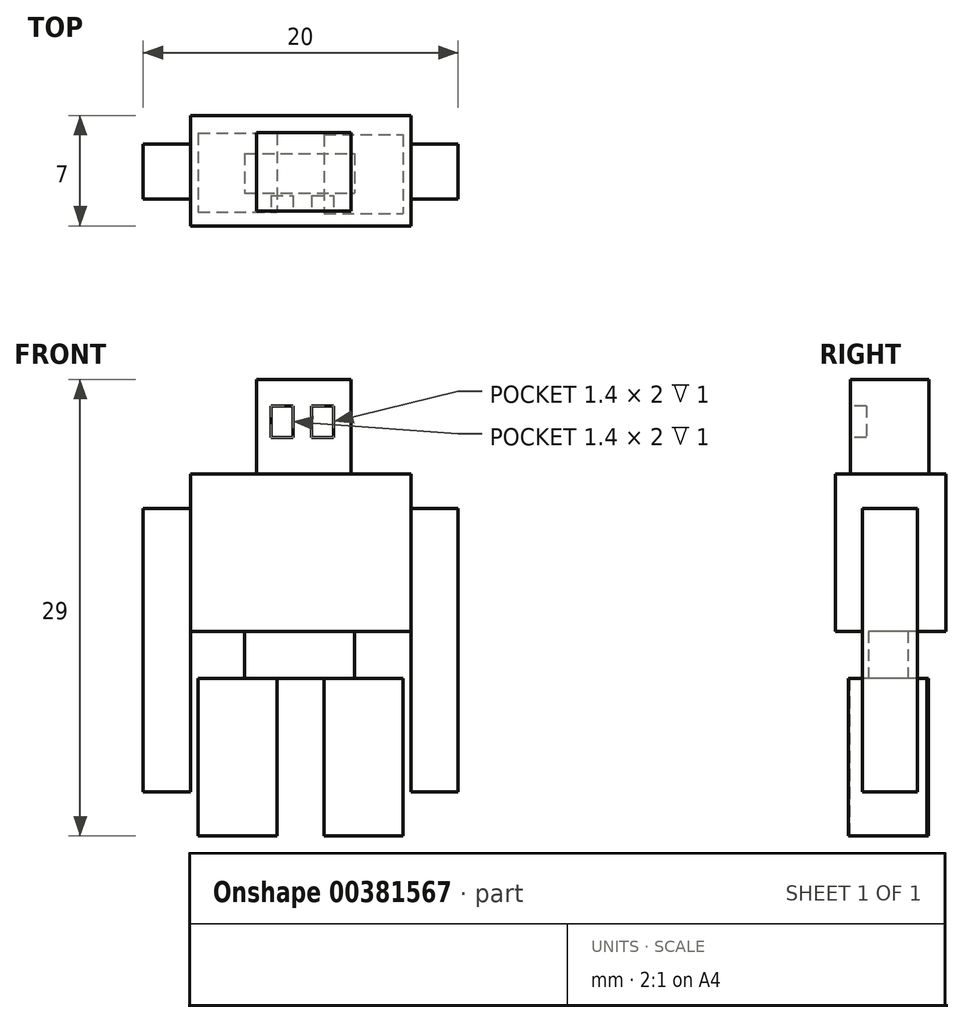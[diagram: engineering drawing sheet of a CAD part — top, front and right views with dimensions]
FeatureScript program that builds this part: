
annotation { "Feature Type Name" : "Feature", "Feature Type Description" : "" }
export const myFeature = defineFeature(function(context is Context, id is Id, definition is map)
    precondition{}
    {
        {
            var Q0;
            Q0=qCreatedBy(makeId("Top.planeOp"),FACE);
            var sketch = newSketch(context, id + "F0", { "sketchPlane" : qUnion([Q0])});
            skLineSegment(sketch, "E0.bottom", {"start": v(-17, -1.9) * mm, "end": v(-12, -1.9) * mm});
            skLineSegment(sketch, "E0.top", {"start": v(-17, -6.9) * mm, "end": v(-12, -6.9) * mm});
            skLineSegment(sketch, "E0.left", {"start": v(-17, -1.9) * mm, "end": v(-17, -6.9) * mm});
            skLineSegment(sketch, "E0.right", {"start": v(-12, -1.9) * mm, "end": v(-12, -6.9) * mm});
            skLineSegment(sketch, "E1.bottom", {"start": v(-9, -2) * mm, "end": v(-4, -2) * mm});
            skLineSegment(sketch, "E1.top", {"start": v(-9, -7) * mm, "end": v(-4, -7) * mm});
            skLineSegment(sketch, "E1.left", {"start": v(-9, -2) * mm, "end": v(-9, -7) * mm});
            skLineSegment(sketch, "E1.right", {"start": v(-4, -2) * mm, "end": v(-4, -7) * mm});
            skSolve(sketch);
        }
        {
            var Q0;
            Q0=makeQuery(id+"F0.imprint","IMPRINT",FACE,{"disambiguationData":[TD([[makeQuery(id+"F0.imprint","IMPRINT",EDGE,{"derivedFrom":sQuery(id+"F0.wireOp",EDGE,"E0.bottom")}),-1.0]])]});
            var Q1;
            Q1=makeQuery(id+"F0.imprint","IMPRINT",FACE,{"disambiguationData":[TD([[makeQuery(id+"F0.imprint","IMPRINT",EDGE,{"derivedFrom":sQuery(id+"F0.wireOp",EDGE,"E1.bottom")}),-1.0]])]});
            extrude(context, id + "F1", {"entities" : qUnion([Q0, Q1]), "depth" : 10 * mm});
        }
        {
            var Q0;
            Q0=makeQuery(id+"F1.opExtrude","CAP_FACE",FACE,{"disambiguationData":[OSD([sQuery(id+"F0.wireOp",EDGE,"E0.bottom"),sQuery(id+"F0.wireOp",EDGE,"E0.top"),sQuery(id+"F0.wireOp",EDGE,"E0.left"),sQuery(id+"F0.wireOp",EDGE,"E0.right")])],"isStart":false});
            var sketch = newSketch(context, id + "F2", { "sketchPlane" : qUnion([Q0])});
            skLineSegment(sketch, "E2.bottom", {"start": v(-14.07, -3.2) * mm, "end": v(-7.07, -3.2) * mm});
            skLineSegment(sketch, "E2.top", {"start": v(-14.07, -5.7) * mm, "end": v(-7.07, -5.7) * mm});
            skLineSegment(sketch, "E2.left", {"start": v(-14.07, -3.2) * mm, "end": v(-14.07, -5.7) * mm});
            skLineSegment(sketch, "E2.right", {"start": v(-7.07, -3.2) * mm, "end": v(-7.07, -5.7) * mm});
            skSolve(sketch);
        }
        {
            var Q0;
            {var subQ0=sQuery(id+"F2.wireOp",EDGE,"E2.left");Q0=makeQuery(id+"F2.imprint","IMPRINT",FACE,{"disambiguationData":[TD([[makeQuery(id+"F2.imprint","IMPRINT",EDGE,{"derivedFrom":subQ0}),1.0]])]});}
            var Q1;
            {var subQ0=sQuery(id+"F2.wireOp",EDGE,"E2.right");Q1=makeQuery(id+"F2.imprint","IMPRINT",FACE,{"disambiguationData":[TD([[makeQuery(id+"F2.imprint","IMPRINT",EDGE,{"derivedFrom":subQ0}),-1.0]])]});}
            extrude(context, id + "F3", {"entities" : qUnion([Q0, Q1]), "depth" : 3 * mm});
        }
        {
            var Q0;
            Q0=makeQuery(id+"F3.opExtrude","CAP_FACE",FACE,{"disambiguationData":[OSD([sQuery(id+"F2.wireOp",EDGE,"E2.bottom"),sQuery(id+"F2.wireOp",EDGE,"E2.top"),sQuery(id+"F2.wireOp",EDGE,"E2.left"),sQuery(id+"F2.wireOp",EDGE,"E2.right")])],"isStart":false});
            var sketch = newSketch(context, id + "F4", { "sketchPlane" : qUnion([Q0])});
            skLineSegment(sketch, "E3.bottom", {"start": v(-17.5, -0.8) * mm, "end": v(-3.5, -0.8) * mm});
            skLineSegment(sketch, "E3.top", {"start": v(-17.5, -7.8) * mm, "end": v(-3.5, -7.8) * mm});
            skLineSegment(sketch, "E3.left", {"start": v(-17.5, -0.8) * mm, "end": v(-17.5, -7.8) * mm});
            skLineSegment(sketch, "E3.right", {"start": v(-3.5, -0.8) * mm, "end": v(-3.5, -7.8) * mm});
            skSolve(sketch);
        }
        {
            var Q0;
            Q0=makeQuery(id+"F4.imprint","IMPRINT",FACE,{"disambiguationData":[TD([[makeQuery(id+"F4.imprint","IMPRINT",EDGE,{"derivedFrom":sQuery(id+"F4.wireOp",EDGE,"E3.bottom")}),-1.0]])]});
            var Q1;
            Q1=makeQuery(id+"F4.imprint","IMPRINT",FACE,{"disambiguationData":[TD([[makeQuery(id+"F4.imprint","IMPRINT",EDGE,{"derivedFrom":makeQuery(id+"F3.opExtrude","CAP_EDGE",EDGE,{"disambiguationData":[OSD([sQuery(id+"F2.wireOp",EDGE,"E2.bottom")])],"isStart":false})}),-1.0]])]});
            extrude(context, id + "F5", {"entities" : qUnion([Q0, Q1]), "depth" : 10 * mm});
        }
        {
            var Q0;
            Q0=makeQuery(id+"F5.opExtrude","CAP_FACE",FACE,{"disambiguationData":[OSD([sQuery(id+"F4.wireOp",EDGE,"E3.bottom"),sQuery(id+"F4.wireOp",EDGE,"E3.top"),sQuery(id+"F4.wireOp",EDGE,"E3.left"),sQuery(id+"F4.wireOp",EDGE,"E3.right")])],"isStart":false});
            var sketch = newSketch(context, id + "F6", { "sketchPlane" : qUnion([Q0])});
            skLineSegment(sketch, "E4.bottom", {"start": v(-13.31, -1.85) * mm, "end": v(-7.31, -1.85) * mm});
            skLineSegment(sketch, "E4.top", {"start": v(-13.31, -6.85) * mm, "end": v(-7.31, -6.85) * mm});
            skLineSegment(sketch, "E4.left", {"start": v(-13.31, -1.85) * mm, "end": v(-13.31, -6.85) * mm});
            skLineSegment(sketch, "E4.right", {"start": v(-7.31, -1.85) * mm, "end": v(-7.31, -6.85) * mm});
            skSolve(sketch);
        }
        {
            var Q0;
            Q0=makeQuery(id+"F6.imprint","IMPRINT",FACE,{"disambiguationData":[TD([[makeQuery(id+"F6.imprint","IMPRINT",EDGE,{"derivedFrom":sQuery(id+"F6.wireOp",EDGE,"E4.bottom")}),-1.0]])]});
            extrude(context, id + "F7", {"entities" : qUnion([Q0]), "operationType" : NewBodyOperationType.ADD, "depth" : 6 * mm});
        }
        {
            var Q0;
            Q0=makeQuery(id+"F7.opExtrude","SWEPT_FACE",FACE,{"disambiguationData":[OSD([sQuery(id+"F6.wireOp",EDGE,"E4.top")])]});
            var sketch = newSketch(context, id + "F8", { "sketchPlane" : qUnion([Q0])});
            skLineSegment(sketch, "E5.bottom", {"start": v(-12.37, 27.31) * mm, "end": v(-10.97, 27.31) * mm});
            skLineSegment(sketch, "E5.top", {"start": v(-12.37, 25.31) * mm, "end": v(-10.97, 25.31) * mm});
            skLineSegment(sketch, "E5.left", {"start": v(-12.37, 27.31) * mm, "end": v(-12.37, 25.31) * mm});
            skLineSegment(sketch, "E5.right", {"start": v(-10.97, 27.31) * mm, "end": v(-10.97, 25.31) * mm});
            skLineSegment(sketch, "E6.bottom", {"start": v(-9.81, 27.31) * mm, "end": v(-8.41, 27.31) * mm});
            skLineSegment(sketch, "E6.top", {"start": v(-9.81, 25.31) * mm, "end": v(-8.41, 25.31) * mm});
            skLineSegment(sketch, "E6.left", {"start": v(-9.81, 27.31) * mm, "end": v(-9.81, 25.31) * mm});
            skLineSegment(sketch, "E6.right", {"start": v(-8.41, 27.31) * mm, "end": v(-8.41, 25.31) * mm});
            skSolve(sketch);
        }
        {
            var Q0;
            Q0=makeQuery(id+"F8.imprint","IMPRINT",FACE,{"disambiguationData":[TD([[makeQuery(id+"F8.imprint","IMPRINT",EDGE,{"derivedFrom":sQuery(id+"F8.wireOp",EDGE,"E5.bottom")}),-1.0]])]});
            var Q1;
            Q1=makeQuery(id+"F8.imprint","IMPRINT",FACE,{"disambiguationData":[TD([[makeQuery(id+"F8.imprint","IMPRINT",EDGE,{"derivedFrom":sQuery(id+"F8.wireOp",EDGE,"E6.bottom")}),-1.0]])]});
            extrude(context, id + "F9", {"entities" : qUnion([Q0, Q1]), "operationType" : NewBodyOperationType.REMOVE, "oppositeDirection" : true, "depth" : 1 * mm});
        }
        {
            var Q0;
            Q0=makeQuery(id+"F5.opExtrude","SWEPT_FACE",FACE,{"disambiguationData":[OSD([sQuery(id+"F4.wireOp",EDGE,"E3.right")])]});
            var sketch = newSketch(context, id + "F10", { "sketchPlane" : qUnion([Q0])});
            skLineSegment(sketch, "E7.bottom", {"start": v(-6.1, 20.8) * mm, "end": v(-2.6, 20.8) * mm});
            skLineSegment(sketch, "E7.top", {"start": v(-6.1, 2.8) * mm, "end": v(-2.6, 2.8) * mm});
            skLineSegment(sketch, "E7.left", {"start": v(-6.1, 20.8) * mm, "end": v(-6.1, 2.8) * mm});
            skLineSegment(sketch, "E7.right", {"start": v(-2.6, 20.8) * mm, "end": v(-2.6, 2.8) * mm});
            skLineSegment(sketch, "E8.bottom", {"start": v(-2.6, 3.55) * mm, "end": v(-2.6, 3.55) * mm});
            skLineSegment(sketch, "E8.top", {"start": v(-2.6, 4.04) * mm, "end": v(-2.6, 4.04) * mm});
            skLineSegment(sketch, "E8.left", {"start": v(-2.6, 3.55) * mm, "end": v(-2.6, 4.04) * mm});
            skLineSegment(sketch, "E8.right", {"start": v(-2.6, 3.55) * mm, "end": v(-2.6, 4.04) * mm});
            skSolve(sketch);
        }
        {
            var Q0;
            {var subQ0=sQuery(id+"F10.wireOp",EDGE,"E7.bottom");Q0=makeQuery(id+"F10.imprint","IMPRINT",FACE,{"disambiguationData":[TD([[makeQuery(id+"F10.imprint","IMPRINT",EDGE,{"derivedFrom":subQ0}),-1.0]])]});}
            var Q1;
            {var subQ5=sQuery(id+"F10.wireOp",EDGE,"E7.top");Q1=makeQuery(id+"F10.imprint","IMPRINT",FACE,{"disambiguationData":[TD([[makeQuery(id+"F10.imprint","IMPRINT",EDGE,{"derivedFrom":subQ5}),1.0]])]});}
            extrude(context, id + "F11", {"entities" : qUnion([Q0, Q1]), "operationType" : NewBodyOperationType.ADD, "depth" : 3 * mm});
        }
        {
            var Q0;
            Q0=makeQuery(id+"F5.opExtrude","SWEPT_FACE",FACE,{"disambiguationData":[OSD([sQuery(id+"F4.wireOp",EDGE,"E3.left")])]});
            var sketch = newSketch(context, id + "F12", { "sketchPlane" : qUnion([Q0])});
            skLineSegment(sketch, "E9.bottom", {"start": v(2.6, 20.8) * mm, "end": v(6.1, 20.8) * mm});
            skLineSegment(sketch, "E9.top", {"start": v(2.6, 2.8) * mm, "end": v(6.1, 2.8) * mm});
            skLineSegment(sketch, "E9.left", {"start": v(2.6, 20.8) * mm, "end": v(2.6, 2.8) * mm});
            skLineSegment(sketch, "E9.right", {"start": v(6.1, 20.8) * mm, "end": v(6.1, 2.8) * mm});
            skSolve(sketch);
        }
        {
            var Q0;
            {var subQ0=sQuery(id+"F12.wireOp",EDGE,"E9.top");Q0=makeQuery(id+"F12.imprint","IMPRINT",FACE,{"disambiguationData":[TD([[makeQuery(id+"F12.imprint","IMPRINT",EDGE,{"derivedFrom":subQ0}),1.0]])]});}
            var Q1;
            {var subQ0=sQuery(id+"F12.wireOp",EDGE,"E9.bottom");Q1=makeQuery(id+"F12.imprint","IMPRINT",FACE,{"disambiguationData":[TD([[makeQuery(id+"F12.imprint","IMPRINT",EDGE,{"derivedFrom":subQ0}),-1.0]])]});}
            extrude(context, id + "F13", {"entities" : qUnion([Q0, Q1]), "operationType" : NewBodyOperationType.ADD, "depth" : 3 * mm});
        }
    });
